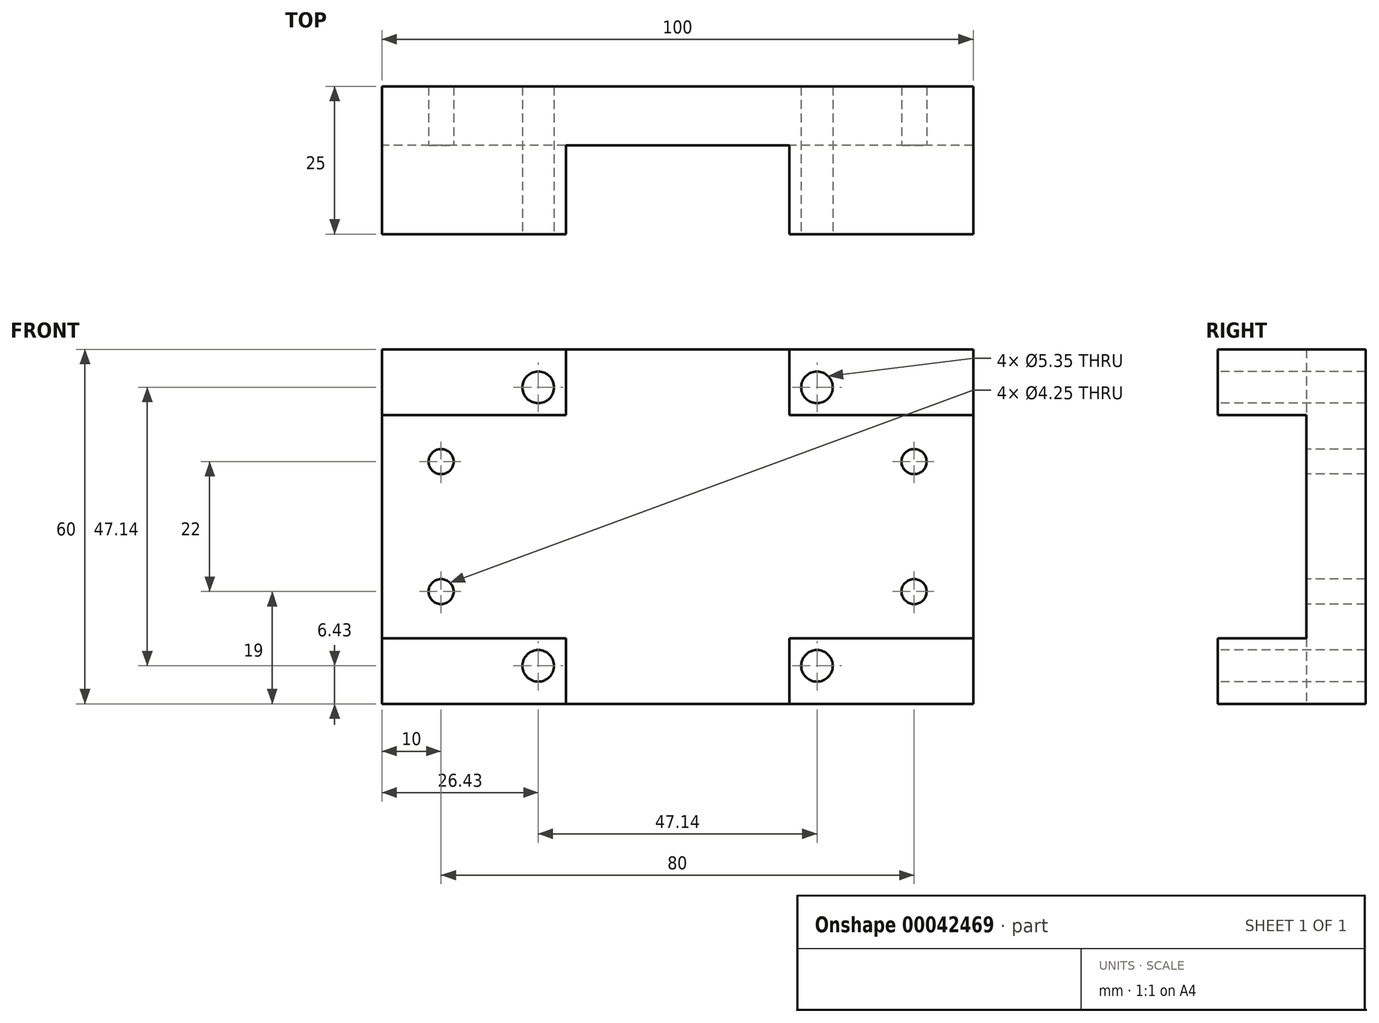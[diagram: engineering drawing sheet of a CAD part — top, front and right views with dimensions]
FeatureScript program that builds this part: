
annotation { "Feature Type Name" : "Feature", "Feature Type Description" : "" }
export const myFeature = defineFeature(function(context is Context, id is Id, definition is map)
    precondition{}
    {
        {
            var Q0;
            Q0=qCreatedBy(makeId("Front.planeOp"),FACE);
            var sketch = newSketch(context, id + "F0", { "sketchPlane" : qUnion([Q0])});
            skLineSegment(sketch, "E0.rect.bottom", {"start": v(50, -30) * mm, "end": v(-50, -30) * mm});
            skLineSegment(sketch, "E0.rect.top", {"start": v(50, 30) * mm, "end": v(-50, 30) * mm});
            skLineSegment(sketch, "E0.rect.left", {"start": v(50, -30) * mm, "end": v(50, 30) * mm});
            skLineSegment(sketch, "E0.rect.right", {"start": v(-50, -30) * mm, "end": v(-50, 30) * mm});
            skPoint(sketch, "E0.rect.middle", {"position": v(0, 0) * mm});
            skSolve(sketch);
        }
        {
            var Q0;
            Q0 = qSketchRegion(id + "F0", true);
            extrude(context, id + "F1", {"entities" : qUnion([Q0]), "depth" : 25 * mm});
        }
        {
            var Q0;
            {var subQ0=sQuery(id+"F0.wireOp",EDGE,"E0.rect.top");var subQ1=sQuery(id+"F0.wireOp",EDGE,"E0.rect.left");var subQ2=sQuery(id+"F0.wireOp",EDGE,"E0.rect.right");Q0=makeQuery(id+"F4.boolean.opBoolean","SPLIT",FACE,{"disambiguationData":[TD([makeQuery(id+"F1.opExtrude","SWEPT_FACE",FACE,{"disambiguationData":[OSD([subQ0])]})])],"derivedFrom":makeQuery(id+"F1.opExtrude","CAP_FACE",FACE,{"disambiguationData":[OSD([sQuery(id+"F0.wireOp",EDGE,"E0.rect.bottom"),subQ0,subQ1,subQ2])],"isStart":false})});}
            var sketch = newSketch(context, id + "F2", { "sketchPlane" : qUnion([Q0])});
            skCircle(sketch, "E1", {"center": v(-23.57, 23.57) * mm, "radius": 2.67 * mm});
            skCircle(sketch, "E2", {"center": v(23.57, 23.57) * mm, "radius": 2.67 * mm});
            skCircle(sketch, "E3", {"center": v(-23.57, -23.57) * mm, "radius": 2.67 * mm});
            skCircle(sketch, "E4", {"center": v(23.57, -23.57) * mm, "radius": 2.67 * mm});
            skSolve(sketch);
        }
        {
            var Q0;
            Q0=makeQuery(id+"F1.opExtrude","CAP_FACE",FACE,{"disambiguationData":[OSD([sQuery(id+"F0.wireOp",EDGE,"E0.rect.bottom"),sQuery(id+"F0.wireOp",EDGE,"E0.rect.top"),sQuery(id+"F0.wireOp",EDGE,"E0.rect.left"),sQuery(id+"F0.wireOp",EDGE,"E0.rect.right")])],"isStart":false});
            var sketch = newSketch(context, id + "F3", { "sketchPlane" : qUnion([Q0])});
            skLineSegment(sketch, "E5.rect.bottom", {"start": v(50, -18.9) * mm, "end": v(-50, -18.9) * mm});
            skLineSegment(sketch, "E5.rect.top", {"start": v(50, 18.9) * mm, "end": v(-50, 18.9) * mm});
            skLineSegment(sketch, "E5.rect.left", {"start": v(50, -18.9) * mm, "end": v(50, 18.9) * mm});
            skLineSegment(sketch, "E5.rect.right", {"start": v(-50, -18.9) * mm, "end": v(-50, 18.9) * mm});
            skPoint(sketch, "E5.rect.middle", {"position": v(0, 0) * mm});
            skSolve(sketch);
        }
        {
            var Q0;
            Q0 = qSketchRegion(id + "F3", true);
            extrude(context, id + "F4", {"entities" : qUnion([Q0]), "operationType" : NewBodyOperationType.REMOVE, "oppositeDirection" : true, "depth" : 15 * mm});
        }
        {
            var Q0;
            Q0 = qSketchRegion(id + "F2", true);
            extrude(context, id + "F5", {"entities" : qUnion([Q0]), "operationType" : NewBodyOperationType.REMOVE, "endBound" : BoundingType.THROUGH_ALL, "oppositeDirection" : true, "depth" : 25 * mm});
        }
        {
            var Q0;
            Q0=makeQuery(id+"FJNhN70Pm0I1sjB_1.boolean.opBoolean","MERGE",FACE,{"derivedFrom":[makeQuery(id+"F4.boolean.opBoolean","COPY",FACE,{"derivedFrom":makeQuery(id+"F4.opExtrude","CAP_FACE",FACE,{"disambiguationData":[OSD([sQuery(id+"F3.wireOp",EDGE,"E5.rect.bottom"),sQuery(id+"F3.wireOp",EDGE,"E5.rect.top"),sQuery(id+"F3.wireOp",EDGE,"E5.rect.left"),sQuery(id+"F3.wireOp",EDGE,"E5.rect.right")])],"isStart":false})}),makeQuery(id+"FJNhN70Pm0I1sjB_1.opExtrude","CAP_FACE",FACE,{"disambiguationData":[OSD([sQuery(id+"FHI85r1Fz0DfBSI_1.wireOp",EDGE,"cb9b67fa-2a52-45c6-ab9f-c01db241dd37")])],"isStart":false})]});
            var sketch = newSketch(context, id + "F6", { "sketchPlane" : qUnion([Q0])});
            skCircle(sketch, "E6", {"center": v(-40, 11) * mm, "radius": 2.12 * mm});
            skCircle(sketch, "E7", {"center": v(-40, -11) * mm, "radius": 2.12 * mm});
            skCircle(sketch, "E8", {"center": v(40, 11) * mm, "radius": 2.12 * mm});
            skCircle(sketch, "E9", {"center": v(40, -11) * mm, "radius": 2.12 * mm});
            skSolve(sketch);
        }
        {
            var Q0;
            Q0 = qSketchRegion(id + "F6", true);
            extrude(context, id + "F7", {"entities" : qUnion([Q0]), "operationType" : NewBodyOperationType.REMOVE, "endBound" : BoundingType.THROUGH_ALL, "oppositeDirection" : true, "depth" : 25 * mm});
        }
        {
            var Q0;
            {var subQ0=sQuery(id+"F0.wireOp",EDGE,"E0.rect.top");var subQ1=sQuery(id+"F0.wireOp",EDGE,"E0.rect.left");var subQ2=sQuery(id+"F0.wireOp",EDGE,"E0.rect.right");Q0=makeQuery(id+"F4.boolean.opBoolean","SPLIT",FACE,{"disambiguationData":[TD([makeQuery(id+"F1.opExtrude","SWEPT_FACE",FACE,{"disambiguationData":[OSD([subQ0])]})])],"derivedFrom":makeQuery(id+"F1.opExtrude","CAP_FACE",FACE,{"disambiguationData":[OSD([sQuery(id+"F0.wireOp",EDGE,"E0.rect.bottom"),subQ0,subQ1,subQ2])],"isStart":false})});}
            var sketch = newSketch(context, id + "F8", { "sketchPlane" : qUnion([Q0])});
            skCircle(sketch, "E10", {"center": v(0, 0) * mm, "radius": 26 * mm, "construction": true});
            skLineSegment(sketch, "E11.rect.bottom", {"start": v(-18.9, 30) * mm, "end": v(18.9, 30) * mm});
            skLineSegment(sketch, "E11.rect.top", {"start": v(-18.9, -30) * mm, "end": v(18.9, -30) * mm});
            skLineSegment(sketch, "E11.rect.left", {"start": v(-18.9, 30) * mm, "end": v(-18.9, -30) * mm});
            skLineSegment(sketch, "E11.rect.right", {"start": v(18.9, 30) * mm, "end": v(18.9, -30) * mm});
            skSolve(sketch);
        }
        {
            var Q0;
            Q0 = qSketchRegion(id + "F8", true);
            extrude(context, id + "F9", {"entities" : qUnion([Q0]), "operationType" : NewBodyOperationType.REMOVE, "oppositeDirection" : true, "depth" : 15 * mm});
        }
    });
